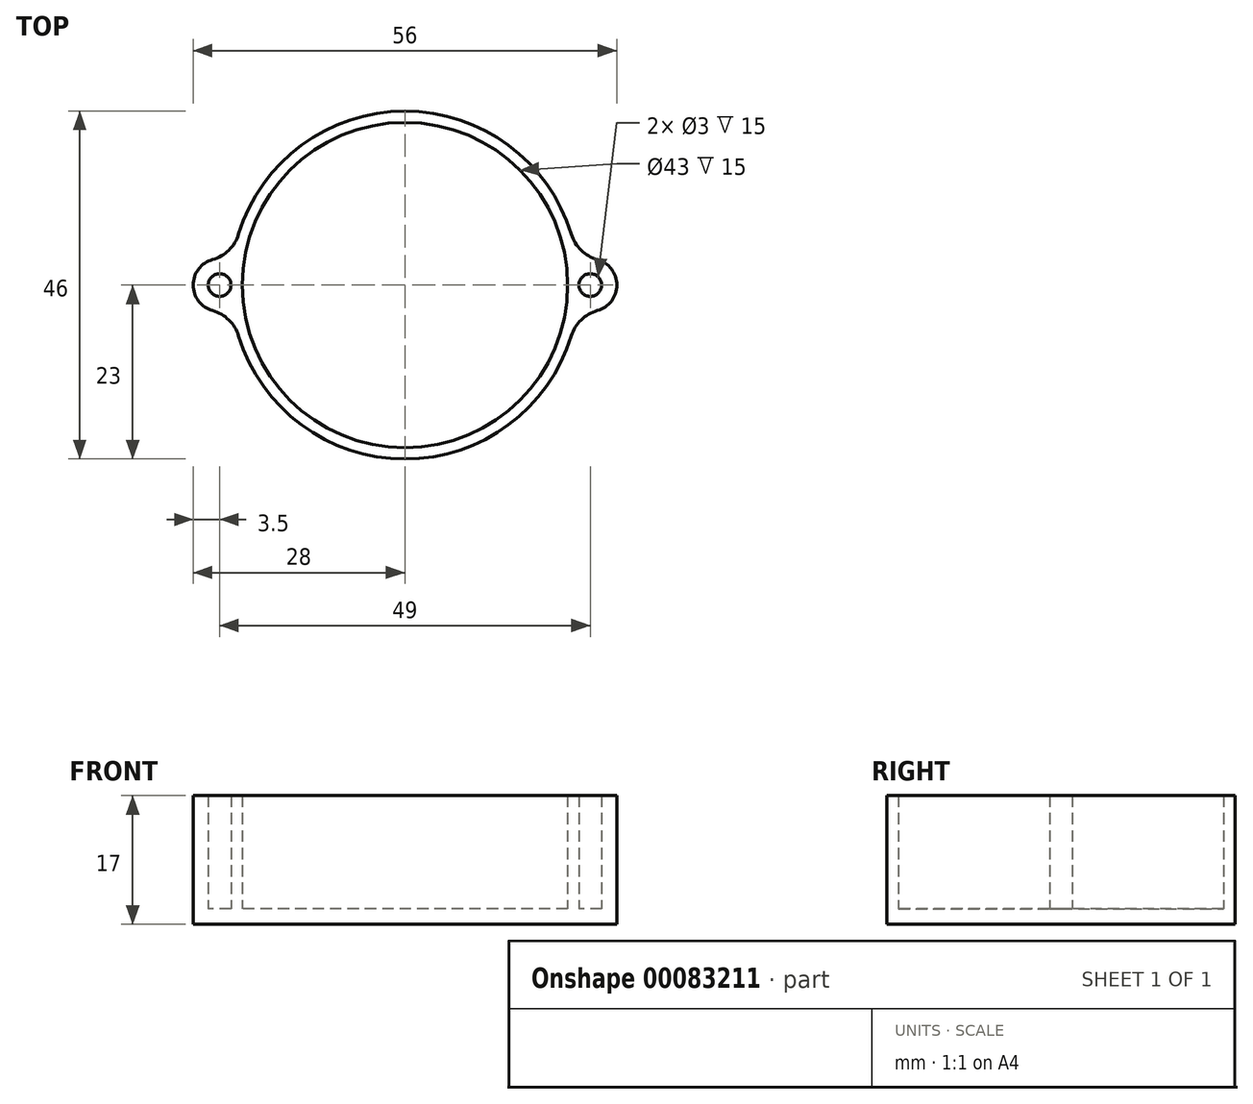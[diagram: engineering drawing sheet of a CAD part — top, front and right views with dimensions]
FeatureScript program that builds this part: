
annotation { "Feature Type Name" : "Feature", "Feature Type Description" : "" }
export const myFeature = defineFeature(function(context is Context, id is Id, definition is map)
    precondition{}
    {
        {
            var Q0;
            Q0=qCreatedBy(makeId("Top.planeOp"),FACE);
            var sketch = newSketch(context, id + "F0", { "sketchPlane" : qUnion([Q0])});
            skCircle(sketch, "E0", {"center": v(0, 0) * mm, "radius": 21.5 * mm});
            skCircle(sketch, "E1.0", {"center": v(0, 0) * mm, "radius": 23 * mm});
            skLineSegment(sketch, "E2", {"start": v(0, 0) * mm, "end": v(-30.1, 0) * mm, "construction": true});
            skLineSegment(sketch, "E3", {"start": v(-30.1, 0) * mm, "end": v(34.9, 0) * mm, "construction": true});
            skCircle(sketch, "E4", {"center": v(-24.5, 0) * mm, "radius": 1.5 * mm});
            skCircle(sketch, "E5", {"center": v(24.5, 0) * mm, "radius": 1.5 * mm});
            skCircle(sketch, "E6.0", {"center": v(24.5, 0) * mm, "radius": 3.5 * mm});
            skCircle(sketch, "E7.0", {"center": v(-24.5, 0) * mm, "radius": 3.5 * mm});
            skSolve(sketch);
        }
        {
            var Q0;
            Q0 = qSketchRegion(id + "F0", true);
            extrude(context, id + "F1", {"entities" : qUnion([Q0]), "depth" : 17 * mm});
        }
        {
            var Q0;
            Q0 = qSketchRegion(id + "F0", true);
            var Q1;
            Q1=makeQuery(id+"F0.imprint","IMPRINT",FACE,{"disambiguationData":[TD([[makeQuery(id+"F0.imprint","IMPRINT",EDGE,{"derivedFrom":sQuery(id+"F0.wireOp",EDGE,"E0")}),1.0]])]});
            var Q2;
            {var subQ0=sQuery(id+"F0.wireOp",EDGE,"E7.0");var subQ1=sQuery(id+"F0.wireOp",EDGE,"E0");var subQ2=makeQuery(id+"F0.imprint","INTERSECT",VERTEX,{"disambiguationData":[OD(0.0)],"derivedFrom":[subQ1,subQ0]});Q2=makeQuery(id+"F0.imprint","IMPRINT",FACE,{"disambiguationData":[TD([[makeQuery(id+"F0.imprint","IMPRINT",EDGE,{"disambiguationData":[TD([[subQ2,-1.0]])],"derivedFrom":subQ1}),1.0]])]});}
            var Q3;
            {var subQ0=sQuery(id+"F0.wireOp",EDGE,"E6.0");var subQ1=sQuery(id+"F0.wireOp",EDGE,"E0");var subQ2=makeQuery(id+"F0.imprint","INTERSECT",VERTEX,{"disambiguationData":[OD(0.0)],"derivedFrom":[subQ1,subQ0]});Q3=makeQuery(id+"F0.imprint","IMPRINT",FACE,{"disambiguationData":[TD([[makeQuery(id+"F0.imprint","IMPRINT",EDGE,{"disambiguationData":[TD([[subQ2,1.0]])],"derivedFrom":subQ1}),1.0]])]});}
            var Q4;
            Q4=makeQuery(id+"F0.imprint","IMPRINT",FACE,{"disambiguationData":[TD([[makeQuery(id+"F0.imprint","IMPRINT",EDGE,{"derivedFrom":sQuery(id+"F0.wireOp",EDGE,"E4")}),1.0]])]});
            var Q5;
            Q5=makeQuery(id+"F0.imprint","IMPRINT",FACE,{"disambiguationData":[TD([[makeQuery(id+"F0.imprint","IMPRINT",EDGE,{"derivedFrom":sQuery(id+"F0.wireOp",EDGE,"E5")}),1.0]])]});
            extrude(context, id + "F2", {"entities" : qUnion([Q0, Q1, Q2, Q3, Q4, Q5]), "operationType" : NewBodyOperationType.ADD, "depth" : 2 * mm});
        }
        {
            var Q0;
            {var subQ0=sQuery(id+"F0.wireOp",EDGE,"E7.0");var subQ1=sQuery(id+"F0.wireOp",EDGE,"E1.0");Q0=makeQuery(id+"F1.opExtrude","SWEPT_EDGE",EDGE,{"disambiguationData":[OSD([subQ1,subQ0]),TDD([makeQuery(id+"F0.imprint","INTERSECT",VERTEX,{"disambiguationData":[OD(0.0)],"derivedFrom":[subQ1,subQ0]})])]});}
            var Q1;
            {var subQ0=sQuery(id+"F0.wireOp",EDGE,"E7.0");var subQ1=sQuery(id+"F0.wireOp",EDGE,"E1.0");Q1=makeQuery(id+"F1.opExtrude","SWEPT_EDGE",EDGE,{"disambiguationData":[OSD([subQ1,subQ0]),TDD([makeQuery(id+"F0.imprint","INTERSECT",VERTEX,{"disambiguationData":[OD(1.0)],"derivedFrom":[subQ1,subQ0]})])]});}
            var Q2;
            {var subQ0=sQuery(id+"F0.wireOp",EDGE,"E6.0");var subQ1=sQuery(id+"F0.wireOp",EDGE,"E1.0");Q2=makeQuery(id+"F1.opExtrude","SWEPT_EDGE",EDGE,{"disambiguationData":[OSD([subQ1,subQ0]),TDD([makeQuery(id+"F0.imprint","INTERSECT",VERTEX,{"disambiguationData":[OD(1.0)],"derivedFrom":[subQ1,subQ0]})])]});}
            var Q3;
            {var subQ0=sQuery(id+"F0.wireOp",EDGE,"E6.0");var subQ1=sQuery(id+"F0.wireOp",EDGE,"E1.0");Q3=makeQuery(id+"F1.opExtrude","SWEPT_EDGE",EDGE,{"disambiguationData":[OSD([subQ1,subQ0]),TDD([makeQuery(id+"F0.imprint","INTERSECT",VERTEX,{"disambiguationData":[OD(0.0)],"derivedFrom":[subQ1,subQ0]})])]});}
            fillet(context, id + "F3", {"entities" : qUnion([Q0, Q1, Q2, Q3]), "radius" : 5 * mm, "tangentPropagation" : true, "allowEdgeOverflow" : false});
        }
    });
